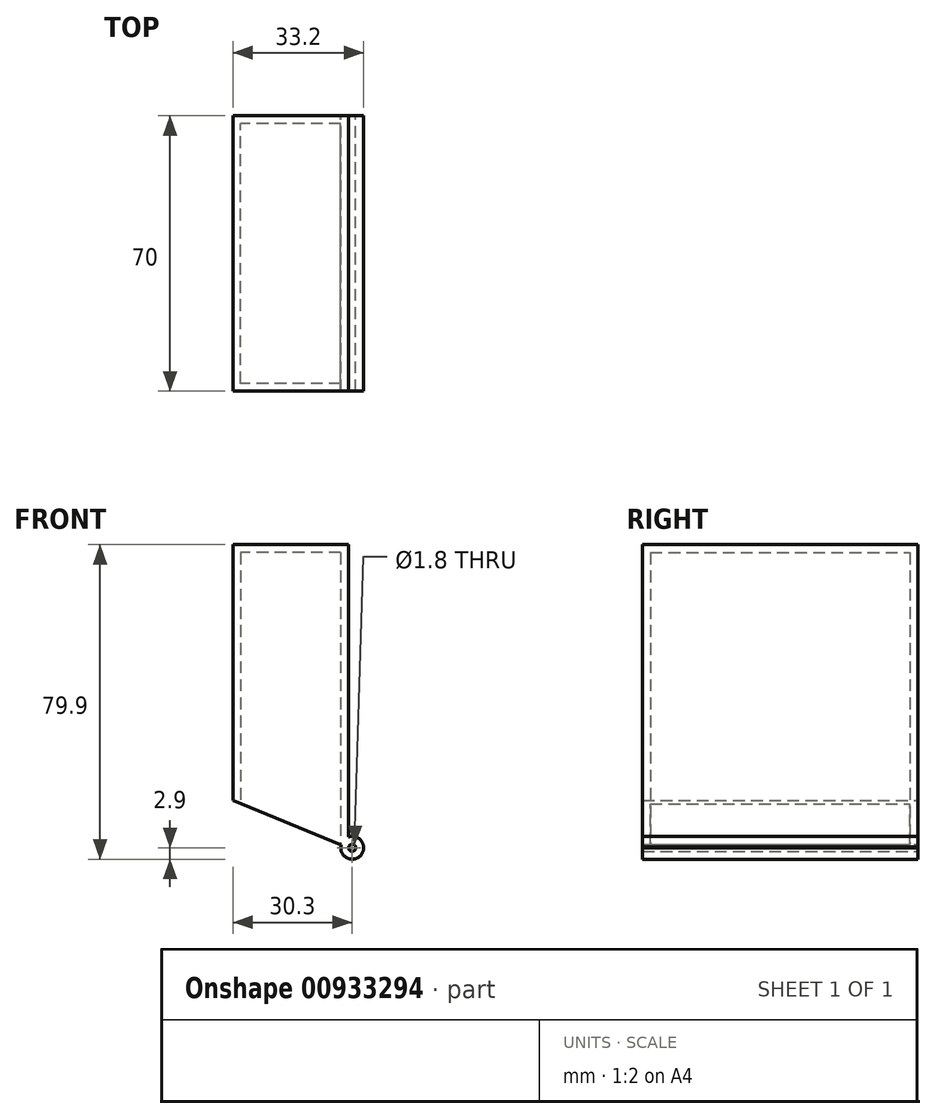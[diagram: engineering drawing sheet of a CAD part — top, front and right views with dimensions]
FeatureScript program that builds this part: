
annotation { "Feature Type Name" : "Feature", "Feature Type Description" : "" }
export const myFeature = defineFeature(function(context is Context, id is Id, definition is map)
    precondition{}
    {
        {
            var Q0;
            Q0=qCreatedBy(makeId("Right.planeOp"),FACE);
            var sketch = newSketch(context, id + "F0", { "sketchPlane" : qUnion([Q0])});
            skLineSegment(sketch, "E0.bottom", {"start": v(0, 0) * mm, "end": v(70, 0) * mm});
            skLineSegment(sketch, "E0.top", {"start": v(0, 77) * mm, "end": v(70, 77) * mm});
            skLineSegment(sketch, "E0.left", {"start": v(0, 0) * mm, "end": v(0, 77) * mm});
            skLineSegment(sketch, "E0.right", {"start": v(70, 0) * mm, "end": v(70, 77) * mm});
            skSolve(sketch);
        }
        {
            var Q0;
            Q0=makeQuery(id+"F0.imprint","IMPRINT",FACE,{"disambiguationData":[TD([[makeQuery(id+"F0.imprint","IMPRINT",EDGE,{"derivedFrom":sQuery(id+"F0.wireOp",EDGE,"E0.bottom")}),1.0]])]});
            extrude(context, id + "F1", {"entities" : qUnion([Q0]), "depth" : 29.4 * mm, "offsetDistance" : 25 * mm});
        }
        {
            var Q0;
            Q0=qCreatedBy(makeId("Top.planeOp"),FACE);
            var sketch = newSketch(context, id + "F2", { "sketchPlane" : qUnion([Q0])});
            skLineSegment(sketch, "E1.0", {"start": v(27.4, 68) * mm, "end": v(2, 68) * mm});
            skLineSegment(sketch, "E1.1", {"start": v(27.4, 2) * mm, "end": v(27.4, 68) * mm});
            skLineSegment(sketch, "E1.2", {"start": v(27.4, 2) * mm, "end": v(2, 2) * mm});
            skLineSegment(sketch, "E1.3", {"start": v(2, 2) * mm, "end": v(2, 68) * mm});
            skLineSegment(sketch, "E2.0", {"start": v(-37.48, -37.48) * mm, "end": v(-37.48, 107.48) * mm});
            skLineSegment(sketch, "E2.1", {"start": v(66.88, -37.48) * mm, "end": v(-37.48, -37.48) * mm});
            skLineSegment(sketch, "E2.2", {"start": v(66.88, 107.48) * mm, "end": v(66.88, -37.48) * mm});
            skLineSegment(sketch, "E2.3", {"start": v(-37.48, 107.48) * mm, "end": v(66.88, 107.48) * mm});
            skSolve(sketch);
        }
        {
            var Q0;
            Q0=makeQuery(id+"F2.imprint","IMPRINT",FACE,{"disambiguationData":[TD([[makeQuery(id+"F2.imprint","IMPRINT",EDGE,{"derivedFrom":sQuery(id+"F2.wireOp",EDGE,"E1.0")}),1.0]])]});
            extrude(context, id + "F3", {"entities" : qUnion([Q0]), "operationType" : NewBodyOperationType.REMOVE, "depth" : 75 * mm, "offsetDistance" : 25 * mm});
        }
        {
            var Q0;
            Q0=makeQuery(id+"F1.opExtrude","SWEPT_FACE",FACE,{"disambiguationData":[OSD([sQuery(id+"F0.wireOp",EDGE,"E0.right")])]});
            var sketch = newSketch(context, id + "F4", { "sketchPlane" : qUnion([Q0])});
            skLineSegment(sketch, "E3", {"start": v(0, 0) * mm, "end": v(0, 12) * mm, "construction": true});
            skLineSegment(sketch, "E4", {"start": v(0, 12) * mm, "end": v(-29.4, 0) * mm});
            skSolve(sketch);
        }
        {
            var Q0;
            {var subQ0=sQuery(id+"F4.wireOp",EDGE,"E4");Q0=makeQuery(id+"F4.imprint","IMPRINT",FACE,{"disambiguationData":[TD([[makeQuery(id+"F4.imprint","IMPRINT",EDGE,{"derivedFrom":subQ0}),1.0]])]});}
            var Q1;
            Q1=makeQuery(id+"F1.opExtrude","SWEPT_FACE",FACE,{"disambiguationData":[OSD([sQuery(id+"F0.wireOp",EDGE,"E0.left")])]});
            extrude(context, id + "F5", {"entities" : qUnion([Q0]), "operationType" : NewBodyOperationType.REMOVE, "endBound" : BoundingType.UP_TO_SURFACE, "oppositeDirection" : true, "depth" : 25 * mm, "endBoundEntityFace" : qUnion([Q1]), "offsetDistance" : 25 * mm});
        }
        {
            var Q0;
            {var subQ0=sQuery(id+"F4.wireOp",EDGE,"E4");Q0=makeQuery(id+"F4.imprint","IMPRINT",FACE,{"disambiguationData":[TD([[makeQuery(id+"F4.imprint","IMPRINT",EDGE,{"derivedFrom":subQ0}),-1.0]])]});}
            var sketch = newSketch(context, id + "F6", { "sketchPlane" : qUnion([Q0])});
            skCircle(sketch, "E5", {"center": v(-30.3, 0) * mm, "radius": 0.9 * mm});
            skCircle(sketch, "E6.0", {"center": v(-30.3, 0) * mm, "radius": 2.9 * mm});
            skLineSegment(sketch, "E7", {"start": v(-33.2, 0) * mm, "end": v(-29.4, 77) * mm});
            skSolve(sketch);
        }
        {
            var Q0;
            Q0=makeQuery(id+"F6.imprint","IMPRINT",FACE,{"disambiguationData":[TD([[makeQuery(id+"F6.imprint","IMPRINT",EDGE,{"derivedFrom":sQuery(id+"F6.wireOp",EDGE,"E5")}),1.0]])]});
            var Q1;
            {var subQ8=sQuery(id+"F6.wireOp",EDGE,"E5");Q1=makeQuery(id+"F6.imprint","IMPRINT",FACE,{"disambiguationData":[TD([[makeQuery(id+"F6.imprint","IMPRINT",EDGE,{"derivedFrom":subQ8}),-1.0]])]});}
            var Q2;
            {var subQ0=sQuery(id+"F6.wireOp",EDGE,"E7");var subQ1=sQuery(id+"F6.wireOp",EDGE,"E6.0");var subQ2=makeQuery(id+"F6.imprint","INTERSECT",VERTEX,{"disambiguationData":[OD(1.0)],"derivedFrom":[subQ1,subQ0]});Q2=makeQuery(id+"F6.imprint","IMPRINT",FACE,{"disambiguationData":[TD([[makeQuery(id+"F6.imprint","IMPRINT",EDGE,{"disambiguationData":[TD([[subQ2,1.0]])],"derivedFrom":subQ1}),-1.0]])]});}
            extrude(context, id + "F7", {"entities" : qUnion([Q0, Q1, Q2]), "operationType" : NewBodyOperationType.ADD, "oppositeDirection" : true, "depth" : 70 * mm, "offsetDistance" : 25 * mm});
        }
        {
            var Q0;
            Q0=makeQuery(id+"F6.imprint","IMPRINT",FACE,{"disambiguationData":[TD([[makeQuery(id+"F6.imprint","IMPRINT",EDGE,{"derivedFrom":sQuery(id+"F6.wireOp",EDGE,"E5")}),1.0]])]});
            var Q1;
            Q1=makeQuery(id+"F7.boolean.opBoolean","MERGE",FACE,{"derivedFrom":[makeQuery(id+"F1.opExtrude","SWEPT_FACE",FACE,{"disambiguationData":[OSD([sQuery(id+"F0.wireOp",EDGE,"E0.left")])]}),makeQuery(id+"F7.opExtrude","CAP_FACE",FACE,{"disambiguationData":[OSD([sQuery(id+"F0.wireOp",EDGE,"E0.right"),sQuery(id+"F4.wireOp",EDGE,"E4"),sQuery(id+"F6.wireOp",EDGE,"E6.0"),sQuery(id+"F6.wireOp",EDGE,"E7")])],"isStart":false})]});
            extrude(context, id + "F8", {"entities" : qUnion([Q0]), "operationType" : NewBodyOperationType.REMOVE, "endBound" : BoundingType.UP_TO_SURFACE, "oppositeDirection" : true, "depth" : 25 * mm, "endBoundEntityFace" : qUnion([Q1]), "offsetDistance" : 25 * mm});
        }
    });
